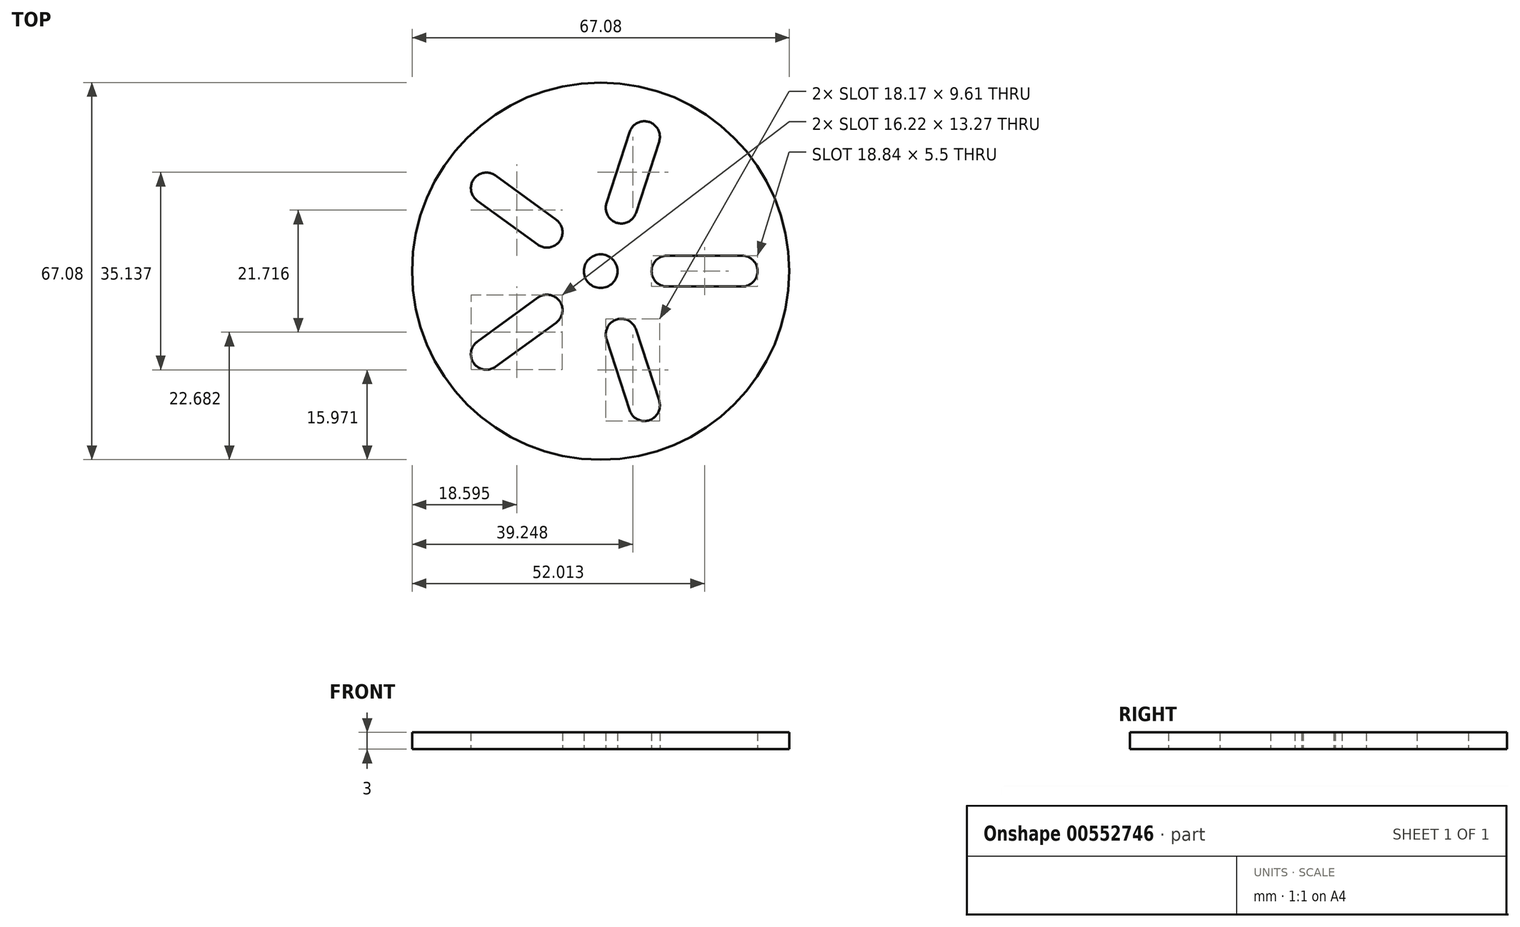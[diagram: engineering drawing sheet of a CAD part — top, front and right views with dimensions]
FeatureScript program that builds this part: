
annotation { "Feature Type Name" : "Feature", "Feature Type Description" : "" }
export const myFeature = defineFeature(function(context is Context, id is Id, definition is map)
    precondition{}
    {
        {
            var Q0;
            Q0=qCreatedBy(makeId("Top.planeOp"),FACE);
            var sketch = newSketch(context, id + "F0", { "sketchPlane" : qUnion([Q0])});
            skLineSegment(sketch, "E0.bottom", {"start": v(0, 75) * mm, "end": v(75, 75) * mm, "construction": true});
            skLineSegment(sketch, "E0.top", {"start": v(0, 0) * mm, "end": v(75, 0) * mm, "construction": true});
            skLineSegment(sketch, "E0.left", {"start": v(0, 75) * mm, "end": v(0, 0) * mm, "construction": true});
            skLineSegment(sketch, "E0.right", {"start": v(75, 75) * mm, "end": v(75, 0) * mm, "construction": true});
            skCircle(sketch, "E1", {"center": v(37.5, 37.5) * mm, "radius": 3 * mm});
            skLineSegment(sketch, "E2", {"start": v(0, 75) * mm, "end": v(37.5, 37.5) * mm, "construction": true});
            skCircle(sketch, "E3", {"center": v(37.5, 37.5) * mm, "radius": 33.54 * mm});
            skLineSegment(sketch, "E4.trimOffspring", {"start": v(35.38, 39.62) * mm, "end": v(75, 0) * mm, "construction": true});
            skPoint(sketch, "E5", {"position": v(18.75, 56.25) * mm});
            skArc(sketch, "E6", {"start": v(49.3, 40.25) * mm, "mid": v(46.55, 37.5) * mm, "end": v(49.3, 34.75) * mm});
            skArc(sketch, "E7", {"start": v(62.64, 34.75) * mm, "mid": v(65.4, 37.5) * mm, "end": v(62.64, 40.25) * mm});
            skLineSegment(sketch, "E8", {"start": v(49.3, 40.25) * mm, "end": v(62.64, 40.25) * mm});
            skLineSegment(sketch, "E9", {"start": v(62.64, 34.75) * mm, "end": v(49.3, 34.75) * mm});
            skArc(sketch, "E10.1.0", {"start": v(47.89, 60.56) * mm, "mid": v(46.12, 64.03) * mm, "end": v(42.65, 62.26) * mm});
            skLineSegment(sketch, "E10.1.1", {"start": v(47.89, 60.56) * mm, "end": v(43.77, 47.88) * mm});
            skLineSegment(sketch, "E10.1.2", {"start": v(38.53, 49.58) * mm, "end": v(42.65, 62.26) * mm});
            skArc(sketch, "E10.1.3", {"start": v(38.53, 49.58) * mm, "mid": v(40.3, 46.11) * mm, "end": v(43.77, 47.88) * mm});
            skArc(sketch, "E10.2.0", {"start": v(18.78, 54.5) * mm, "mid": v(14.94, 53.9) * mm, "end": v(15.54, 50.05) * mm});
            skLineSegment(sketch, "E10.2.1", {"start": v(18.78, 54.5) * mm, "end": v(29.57, 46.67) * mm});
            skLineSegment(sketch, "E10.2.2", {"start": v(26.33, 42.21) * mm, "end": v(15.54, 50.05) * mm});
            skArc(sketch, "E10.2.3", {"start": v(26.33, 42.21) * mm, "mid": v(30.18, 42.82) * mm, "end": v(29.57, 46.67) * mm});
            skArc(sketch, "E10.3.0", {"start": v(15.54, 24.95) * mm, "mid": v(14.94, 21.1) * mm, "end": v(18.78, 20.5) * mm});
            skLineSegment(sketch, "E10.3.1", {"start": v(15.54, 24.95) * mm, "end": v(26.33, 32.79) * mm});
            skLineSegment(sketch, "E10.3.2", {"start": v(29.57, 28.33) * mm, "end": v(18.78, 20.5) * mm});
            skArc(sketch, "E10.3.3", {"start": v(29.57, 28.33) * mm, "mid": v(30.18, 32.18) * mm, "end": v(26.33, 32.79) * mm});
            skArc(sketch, "E10.4.0", {"start": v(42.65, 12.74) * mm, "mid": v(46.12, 10.97) * mm, "end": v(47.89, 14.44) * mm});
            skLineSegment(sketch, "E10.4.1", {"start": v(42.65, 12.74) * mm, "end": v(38.53, 25.42) * mm});
            skLineSegment(sketch, "E10.4.2", {"start": v(43.77, 27.12) * mm, "end": v(47.89, 14.44) * mm});
            skArc(sketch, "E10.4.3", {"start": v(43.77, 27.12) * mm, "mid": v(40.3, 28.89) * mm, "end": v(38.53, 25.42) * mm});
            skSolve(sketch);
        }
        {
            var Q0;
            Q0=makeQuery(id+"F0.imprint","IMPRINT",FACE,{"disambiguationData":[TD([[makeQuery(id+"F0.imprint","IMPRINT",EDGE,{"derivedFrom":sQuery(id+"F0.wireOp",EDGE,"E1")}),-1.0]])]});
            extrude(context, id + "F1", {"entities" : qUnion([Q0]), "depth" : 3 * mm, "offsetDistance" : 25 * mm});
        }
    });
